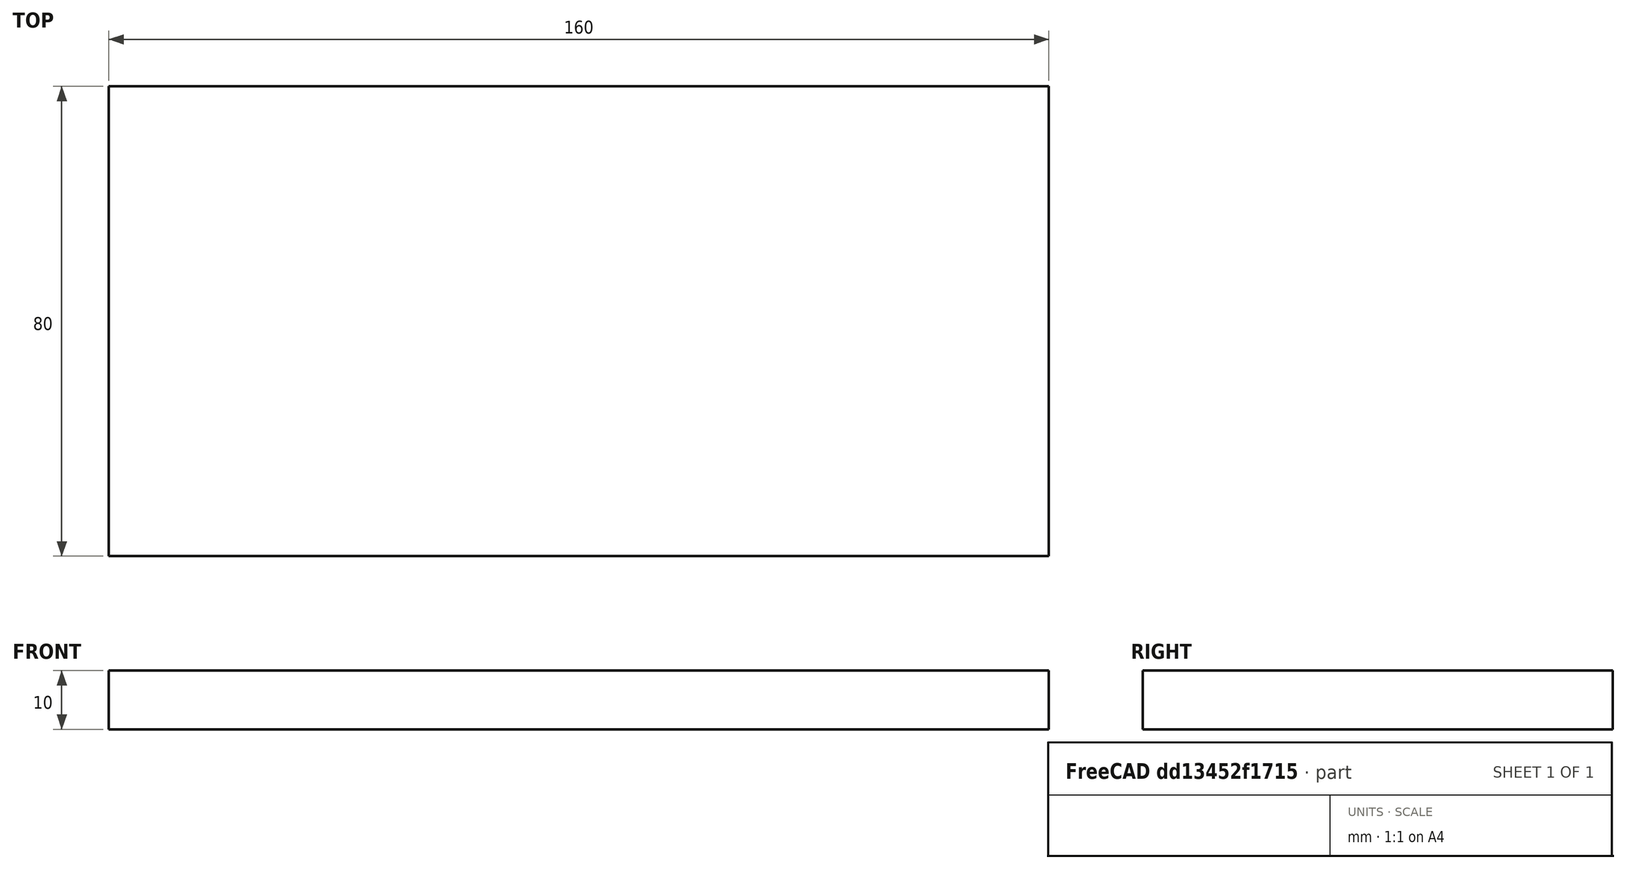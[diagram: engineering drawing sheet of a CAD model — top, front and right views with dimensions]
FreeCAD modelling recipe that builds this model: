
FCSTD DOCUMENT  (FreeCAD 0.18R4 (GitTag))
Label: Divider-D
License: All rights reserved
LicenseURL: http://en.wikipedia.org/wiki/All_rights_reserved
objects: Sketcher::SketchObject×1, PartDesign::Pad×1, PartDesign::Body×1
note: 4 computed .brp shape members not serialized (recipe doc carries the construction recipe); baked Part::Feature solids carry a one-line shape summary decoded from their .brp

FEATURE [Sketcher::SketchObject] Sketch
  MapMode = 5
  Support = -> [XY_Plane]
  sketch-geometry (4):
    g0: LineSegment StartX=0 StartY=0 StartZ=0 EndX=-160 EndY=0 EndZ=0
    g1: LineSegment StartX=-160 StartY=0 StartZ=0 EndX=-160 EndY=80 EndZ=0
    g2: LineSegment StartX=-160 StartY=80 StartZ=0 EndX=0 EndY=80 EndZ=0
    g3: LineSegment StartX=0 StartY=80 StartZ=0 EndX=0 EndY=0 EndZ=0
  constraints (11):
    c: Coincident(g0,g1)
    c: Coincident(g1,g2)
    c: Coincident(g2,g3)
    c: Coincident(g3,g0)
    c: Horizontal(g0)
    c: Horizontal(g2)
    c: Vertical(g1)
    c: Vertical(g3)
    c: Distance(g2) = 160
    c: Distance(g3) = 80
    c: Coincident(g0,g-1)
FEATURE [PartDesign::Pad] Pad
  Length = 10
  Length2 = 100
  Profile = -> Sketch
  Type = 0
FEATURE [PartDesign::Body] Body
  Group = -> [Sketch,Pad]
  Origin = -> Origin
  Tip = -> Pad
